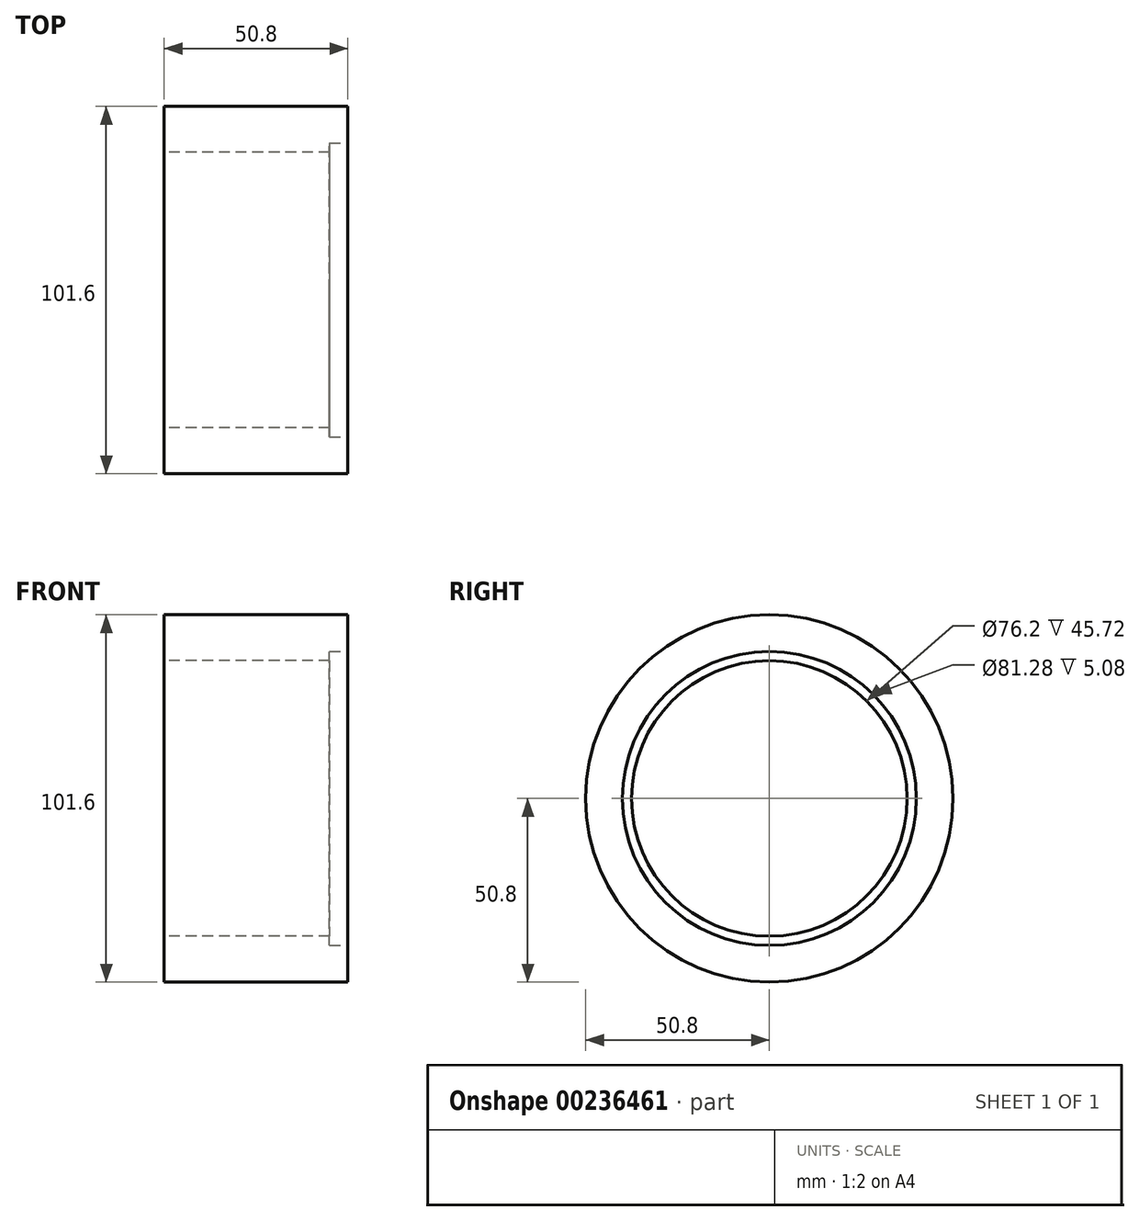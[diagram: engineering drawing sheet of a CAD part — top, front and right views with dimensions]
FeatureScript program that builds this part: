
annotation { "Feature Type Name" : "Feature", "Feature Type Description" : "" }
export const myFeature = defineFeature(function(context is Context, id is Id, definition is map)
    precondition{}
    {
        {
            var Q0;
            Q0=qCreatedBy(makeId("Right.planeOp"),FACE);
            var sketch = newSketch(context, id + "F0", { "sketchPlane" : qUnion([Q0])});
            skCircle(sketch, "E0", {"center": v(0, 0) * mm, "radius": 50.8 * mm});
            skCircle(sketch, "E1.0", {"center": v(0, 0) * mm, "radius": 38.1 * mm});
            skSolve(sketch);
        }
        {
            var Q0;
            Q0=makeQuery(id+"F0.imprint","IMPRINT",FACE,{"disambiguationData":[TD([[makeQuery(id+"F0.imprint","IMPRINT",EDGE,{"derivedFrom":sQuery(id+"F0.wireOp",EDGE,"E0")}),1.0]])]});
            extrude(context, id + "F1", {"entities" : qUnion([Q0]), "depth" : 50.8 * mm});
        }
        {
            var Q0;
            Q0=qCreatedBy(makeId("Front.planeOp"),FACE);
            var sketch = newSketch(context, id + "F2", { "sketchPlane" : qUnion([Q0])});
            skLineSegment(sketch, "E2.bottom", {"start": v(50.8, 40.64) * mm, "end": v(45.72, 40.64) * mm});
            skLineSegment(sketch, "E2.top", {"start": v(50.8, 35.56) * mm, "end": v(45.72, 35.56) * mm});
            skLineSegment(sketch, "E2.left", {"start": v(50.8, 40.64) * mm, "end": v(50.8, 35.56) * mm});
            skLineSegment(sketch, "E2.right", {"start": v(45.72, 40.64) * mm, "end": v(45.72, 35.56) * mm});
            skSolve(sketch);
        }
        {
            var Q0;
            Q0=makeQuery(id+"F2.imprint","IMPRINT",FACE,{"disambiguationData":[TD([[makeQuery(id+"F2.imprint","IMPRINT",EDGE,{"derivedFrom":sQuery(id+"F2.wireOp",EDGE,"E2.bottom")}),1.0]])]});
            var Q1;
            Q1=makeQuery(id+"F1.opExtrude","CAP_EDGE",EDGE,{"disambiguationData":[OSD([sQuery(id+"F0.wireOp",EDGE,"E1.0")])],"isStart":false});
            revolve(context, id + "F3", {"operationType" : NewBodyOperationType.REMOVE, "entities" : qUnion([Q0]), "axis" : qUnion([Q1]), "revolveType" : RevolveType.FULL, "oppositeDirection" : true});
        }
    });
